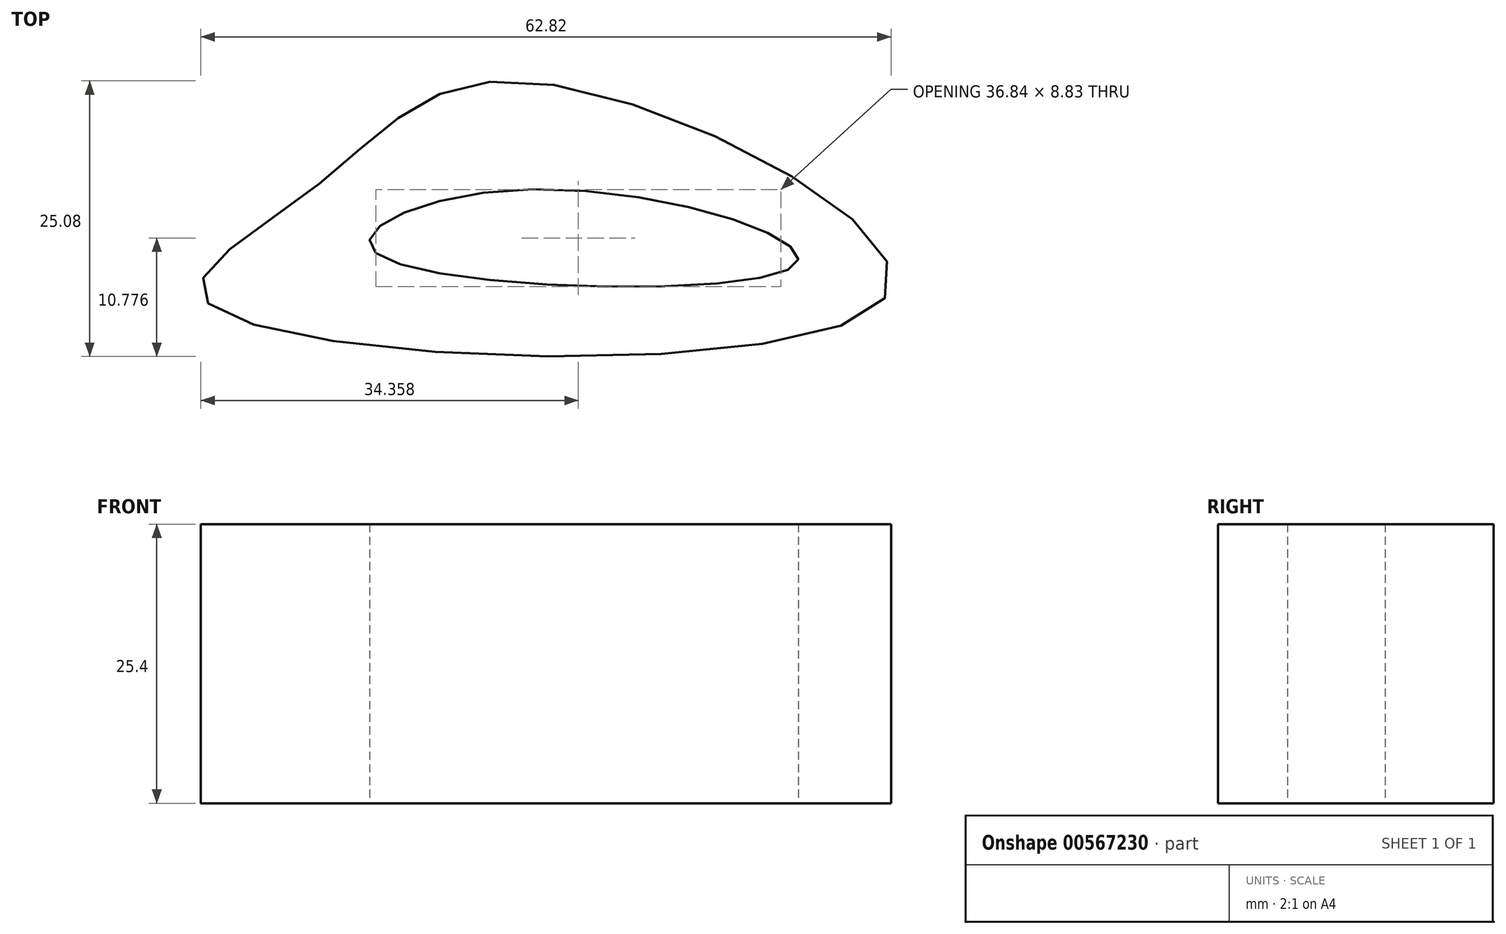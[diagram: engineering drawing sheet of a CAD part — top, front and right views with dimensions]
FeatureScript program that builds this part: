
annotation { "Feature Type Name" : "Feature", "Feature Type Description" : "" }
export const myFeature = defineFeature(function(context is Context, id is Id, definition is map)
    precondition{}
    {
        {
            var Q0;
            Q0=qCreatedBy(makeId("Top.planeOp"),FACE);
            var sketch = newSketch(context, id + "F0", { "sketchPlane" : qUnion([Q0])});
            skFitSpline(sketch, "E0", {"points": [v(-67.49, 31.76) * mm, v(-58.02, 42.14) * mm, v(-38.17, 51.91) * mm, v(-5.8, 32.37) * mm, v(-67.49, 31.76) * mm]});
            skFitSpline(sketch, "E1", {"points": [v(-52.22, 36.34) * mm, v(-38.23, 42.14) * mm, v(-14.13, 35.17) * mm, v(-52.22, 36.34) * mm]});
            skSolve(sketch);
        }
        {
            var Q0;
            Q0=makeQuery(id+"F0.imprint","IMPRINT",FACE,{"disambiguationData":[TD([[makeQuery(id+"F0.imprint","IMPRINT",EDGE,{"derivedFrom":sQuery(id+"F0.wireOp",EDGE,"E0")}),-1.0]])]});
            extrude(context, id + "F1", {"entities" : qUnion([Q0]), "depth" : 25.4 * mm, "offsetDistance" : 25.4 * mm});
        }
    });
